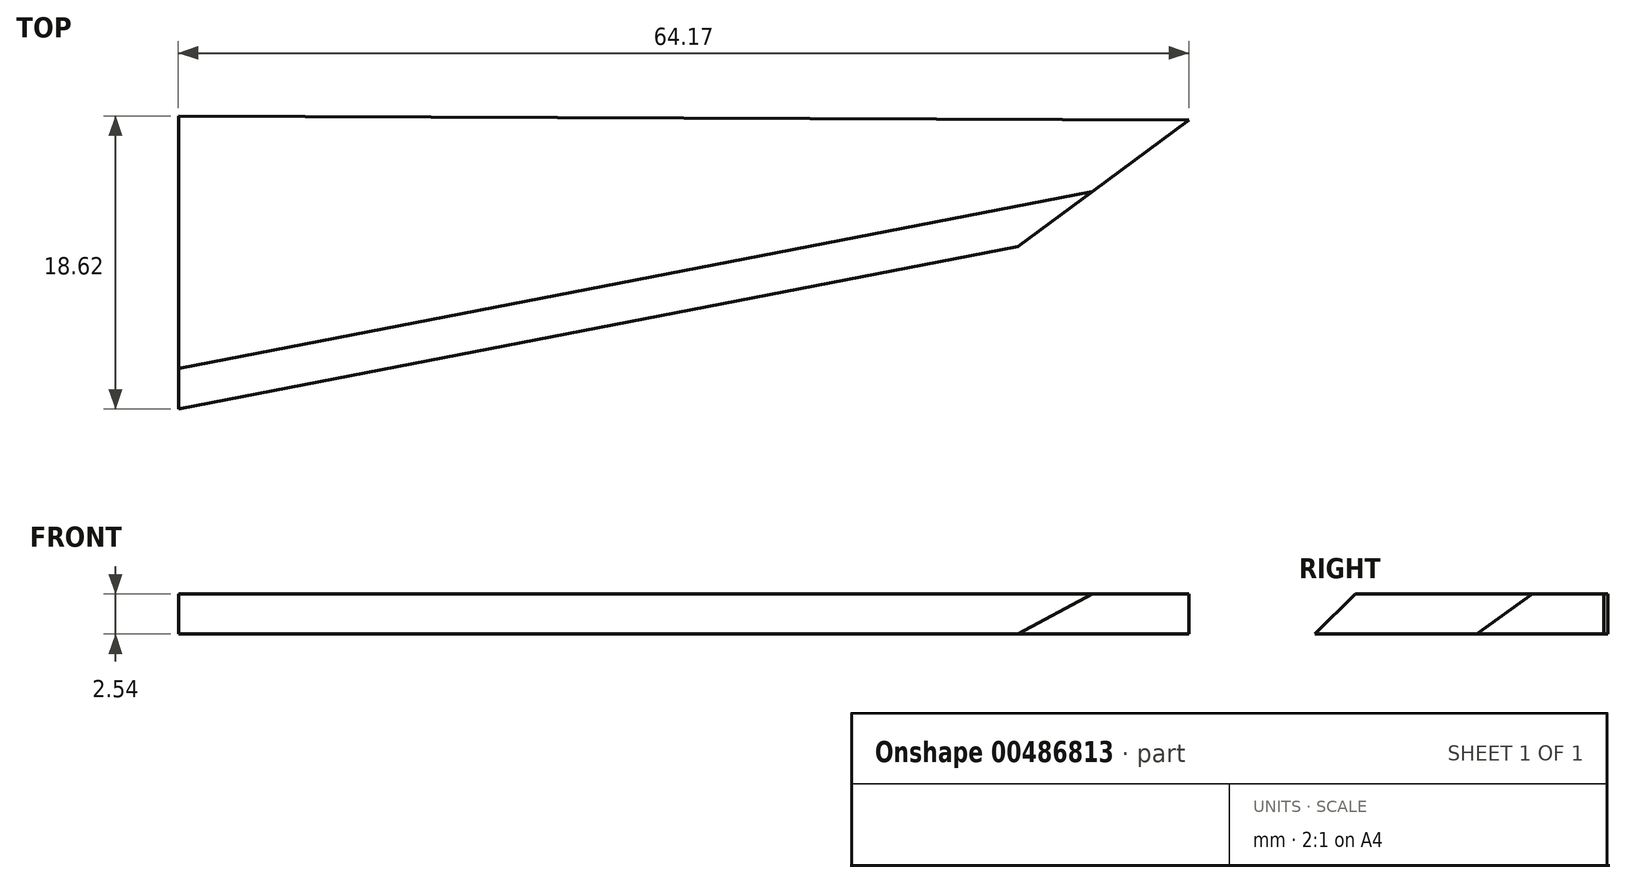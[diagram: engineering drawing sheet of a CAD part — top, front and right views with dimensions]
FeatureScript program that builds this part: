
annotation { "Feature Type Name" : "Feature", "Feature Type Description" : "" }
export const myFeature = defineFeature(function(context is Context, id is Id, definition is map)
    precondition{}
    {
        {
            var Q0;
            Q0=qCreatedBy(makeId("Top.planeOp"),FACE);
            var sketch = newSketch(context, id + "F0", { "sketchPlane" : qUnion([Q0])});
            skLineSegment(sketch, "E0", {"start": v(-42.29, 6.44) * mm, "end": v(-42.29, -14.77) * mm});
            skLineSegment(sketch, "E1", {"start": v(-42.29, -14.77) * mm, "end": v(6.3, -5.37) * mm});
            skLineSegment(sketch, "E2", {"start": v(6.3, -5.37) * mm, "end": v(21.88, 6.18) * mm});
            skLineSegment(sketch, "E3", {"start": v(21.88, 6.18) * mm, "end": v(-42.29, 6.44) * mm});
            skSolve(sketch);
        }
        {
            var Q0;
            Q0=makeQuery(id+"F0.imprint","IMPRINT",FACE,{"disambiguationData":[TD([[makeQuery(id+"F0.imprint","IMPRINT",EDGE,{"derivedFrom":sQuery(id+"F0.wireOp",EDGE,"E0")}),1.0]])]});
            extrude(context, id + "F1", {"entities" : qUnion([Q0]), "depth" : 2.54 * mm, "offsetDistance" : 25.4 * mm});
        }
        {
            var Q0;
            Q0=makeQuery(id+"F1.opExtrude","CAP_EDGE",EDGE,{"disambiguationData":[OSD([sQuery(id+"F0.wireOp",EDGE,"E1")])],"isStart":false});
            chamfer(context, id + "F2", {"entities" : qUnion([Q0]), "width" : 5.08 * mm, "tangentPropagation" : true});
        }
    });
